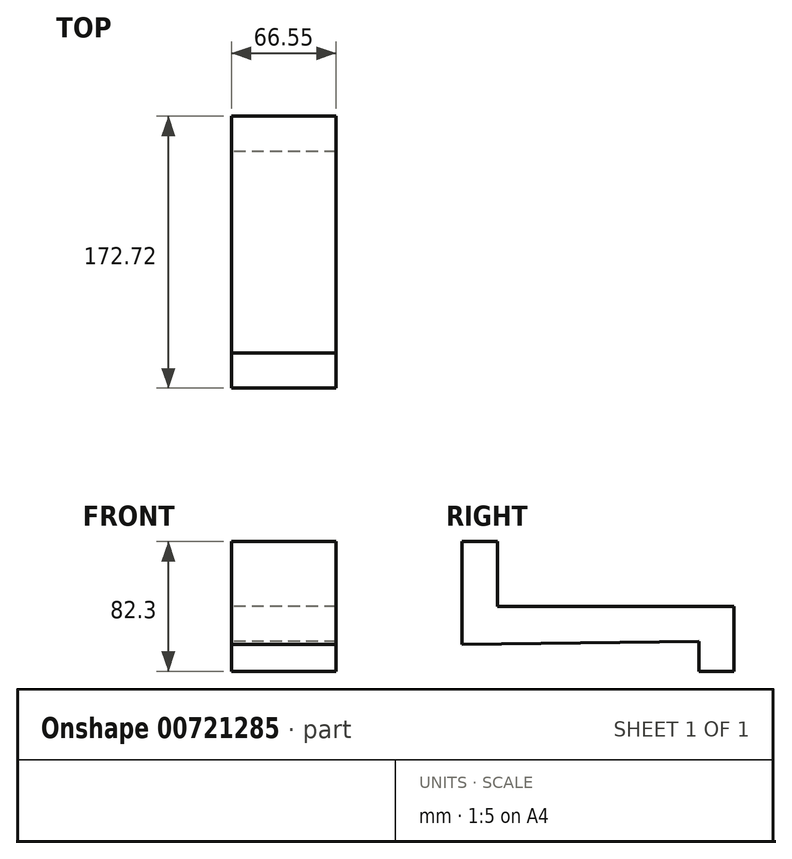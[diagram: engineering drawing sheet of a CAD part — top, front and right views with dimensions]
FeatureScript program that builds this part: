
annotation { "Feature Type Name" : "Feature", "Feature Type Description" : "" }
export const myFeature = defineFeature(function(context is Context, id is Id, definition is map)
    precondition{}
    {
        {
            var Q0;
            Q0=qCreatedBy(makeId("Right.planeOp"),FACE);
            var sketch = newSketch(context, id + "F0", { "sketchPlane" : qUnion([Q0])});
            skLineSegment(sketch, "E0", {"start": v(-65.94, 63.5) * mm, "end": v(-65.94, 0) * mm});
            skSolve(sketch);
        }
        {
            var Q0;
            Q0=qCreatedBy(makeId("Right.planeOp"),FACE);
            var sketch = newSketch(context, id + "F1", { "sketchPlane" : qUnion([Q0])});
            skLineSegment(sketch, "E1", {"start": v(-65.85, 63.5) * mm, "end": v(-43.5, 63.5) * mm});
            skLineSegment(sketch, "E2", {"start": v(-43.5, 63.5) * mm, "end": v(-43.5, 22.35) * mm});
            skLineSegment(sketch, "E3", {"start": v(-43.5, 22.35) * mm, "end": v(106.87, 22.35) * mm});
            skLineSegment(sketch, "E4", {"start": v(106.87, 22.35) * mm, "end": v(106.87, -18.8) * mm});
            skLineSegment(sketch, "E5", {"start": v(106.87, -18.8) * mm, "end": v(84.52, -18.8) * mm});
            skLineSegment(sketch, "E6", {"start": v(84.52, -18.8) * mm, "end": v(84.52, 0) * mm});
            skLineSegment(sketch, "E7", {"start": v(-65.85, 63.5) * mm, "end": v(-65.85, -1.68) * mm});
            skLineSegment(sketch, "E8", {"start": v(-65.85, -1.68) * mm, "end": v(84.52, 0) * mm});
            skSolve(sketch);
        }
        {
            var Q0;
            Q0 = qSketchRegion(id + "F0", true);
            var Q1;
            Q1=makeQuery(id+"F1.imprint","IMPRINT",FACE,{"disambiguationData":[TD([[makeQuery(id+"F1.imprint","IMPRINT",EDGE,{"derivedFrom":sQuery(id+"F1.wireOp",EDGE,"E1")}),-1.0]])]});
            extrude(context, id + "F2", {"entities" : qUnion([Q0, Q1]), "depth" : 66.55 * mm, "offsetDistance" : 25.4 * mm});
        }
    });
